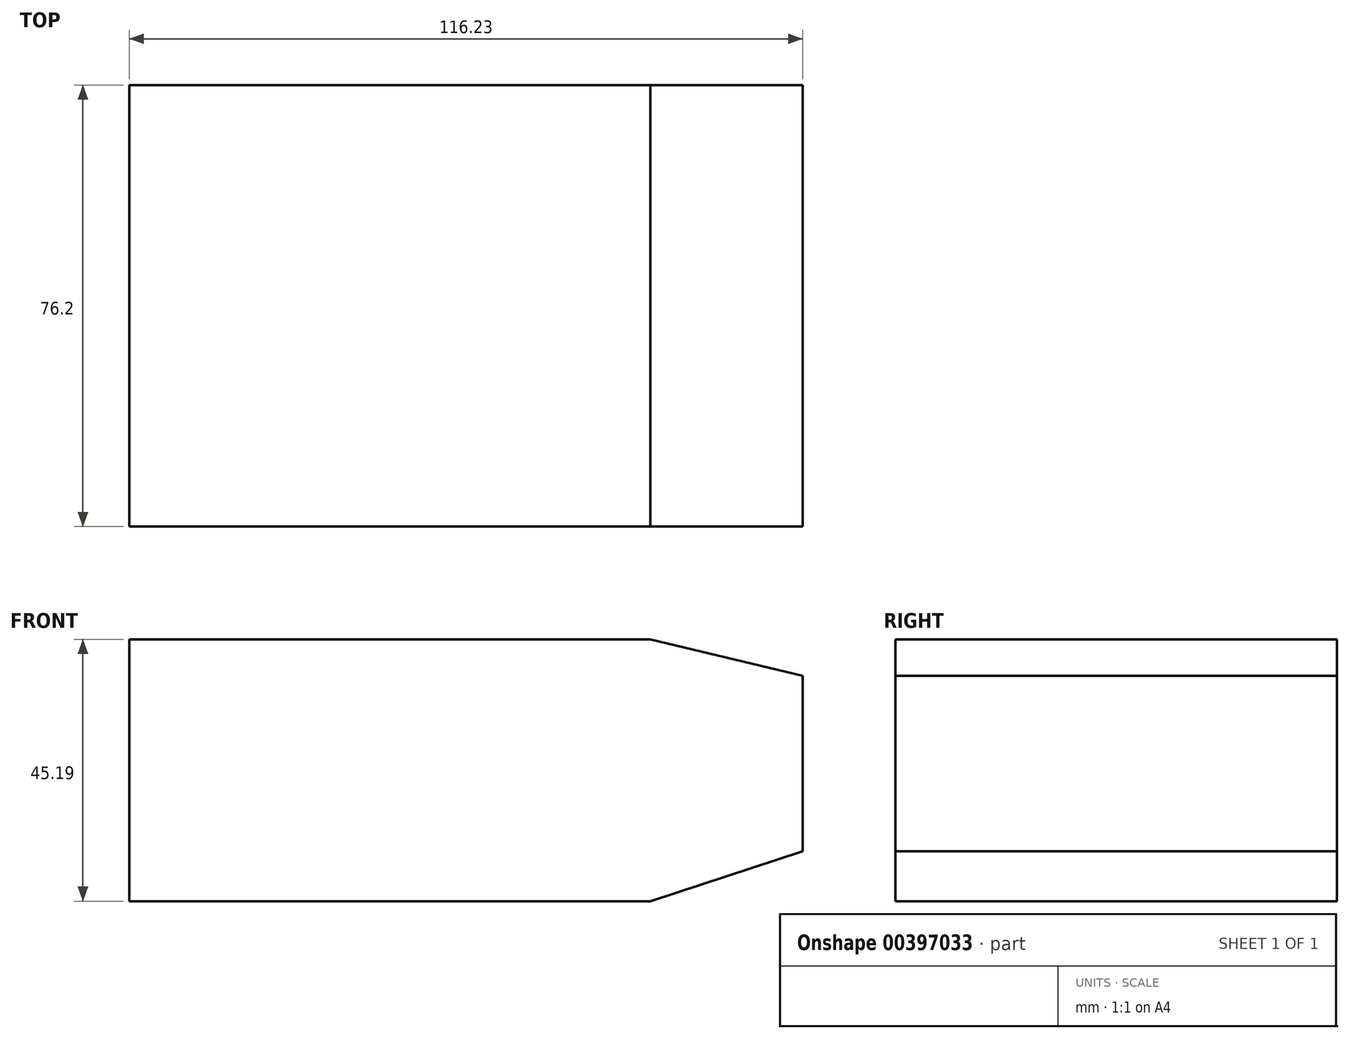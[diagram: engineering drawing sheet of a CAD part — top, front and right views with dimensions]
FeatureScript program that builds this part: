
annotation { "Feature Type Name" : "Feature", "Feature Type Description" : "" }
export const myFeature = defineFeature(function(context is Context, id is Id, definition is map)
    precondition{}
    {
        {
            var Q0;
            Q0=qCreatedBy(makeId("Front.planeOp"),FACE);
            var sketch = newSketch(context, id + "F0", { "sketchPlane" : qUnion([Q0])});
            skLineSegment(sketch, "E0.bottom", {"start": v(-64.47, -18.58) * mm, "end": v(25.44, -18.58) * mm});
            skLineSegment(sketch, "E0.top", {"start": v(-64.47, 26.6) * mm, "end": v(25.44, 26.6) * mm});
            skLineSegment(sketch, "E0.left", {"start": v(-64.47, -18.58) * mm, "end": v(-64.47, 26.6) * mm});
            skLineSegment(sketch, "E0.right", {"start": v(25.44, -18.58) * mm, "end": v(25.44, 26.6) * mm});
            skLineSegment(sketch, "E1", {"start": v(25.44, 26.6) * mm, "end": v(51.76, 20.32) * mm});
            skLineSegment(sketch, "E2", {"start": v(51.76, 20.32) * mm, "end": v(51.76, -9.96) * mm});
            skLineSegment(sketch, "E3", {"start": v(51.76, -9.96) * mm, "end": v(25.44, -18.58) * mm});
            skLineSegment(sketch, "E4", {"start": v(27.98, 26) * mm, "end": v(27.98, 36.4) * mm});
            skLineSegment(sketch, "E5", {"start": v(27.98, -17.75) * mm, "end": v(27.98, -27.43) * mm});
            skPoint(sketch, "E5.startSnap0", {"position": v(27.98, 31.2) * mm});
            skLineSegment(sketch, "E6", {"start": v(-55.15, -18.58) * mm, "end": v(-55.15, -27.43) * mm});
            skLineSegment(sketch, "E7", {"start": v(-57.48, 26.6) * mm, "end": v(-57.48, 36.4) * mm});
            skSolve(sketch);
        }
        {
            var Q0;
            Q0 = qSketchRegion(id + "F0", true);
            extrude(context, id + "F1", {"entities" : qUnion([Q0]), "depth" : 76.2 * mm});
        }
    });
